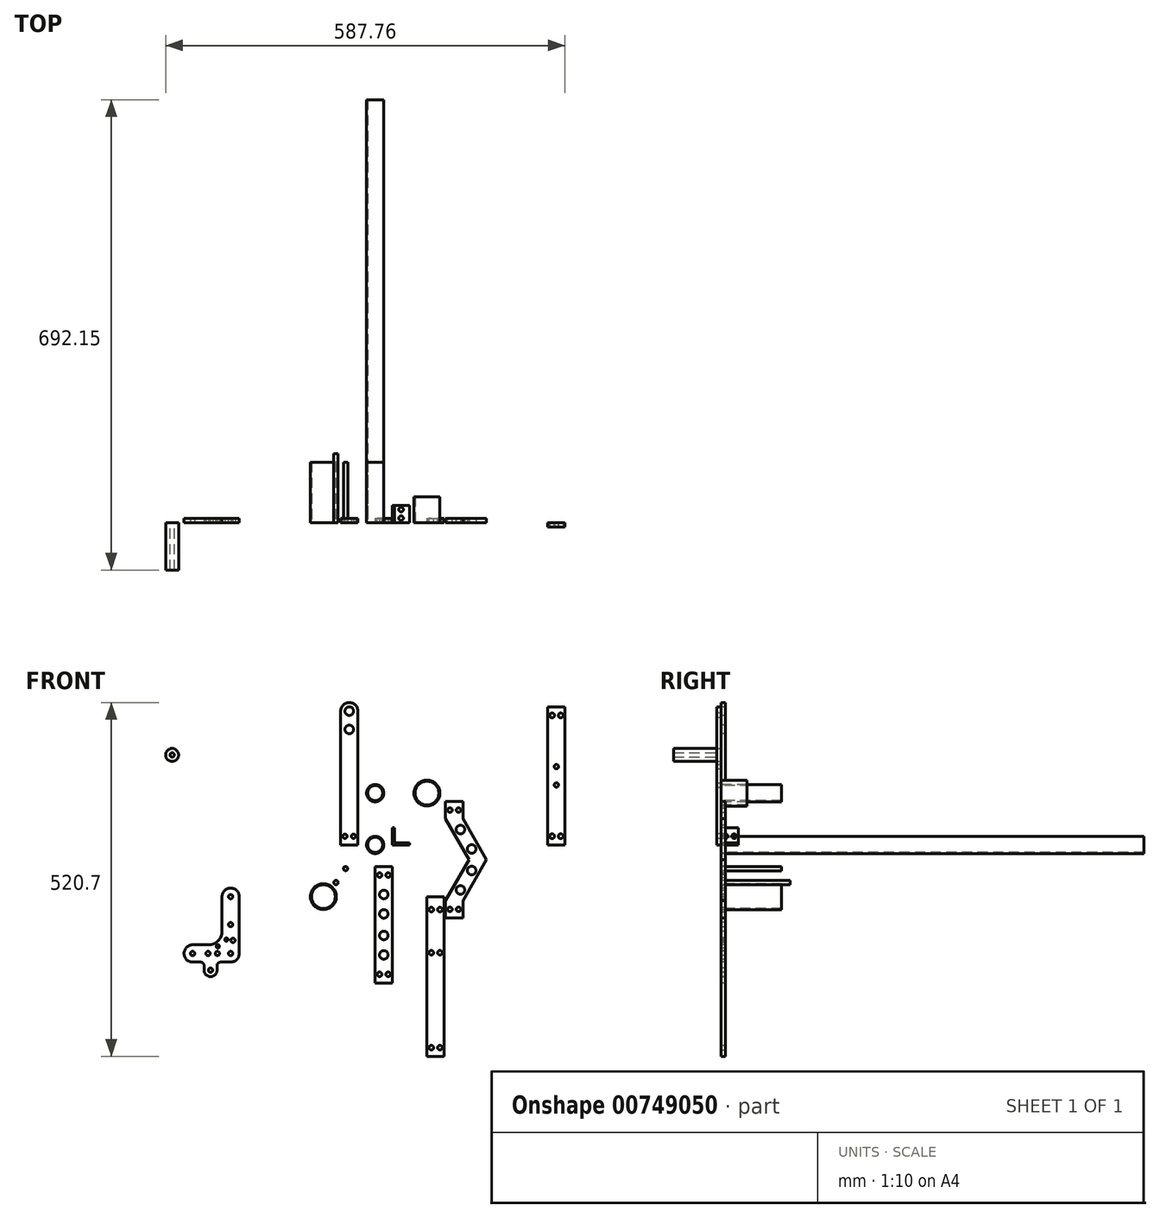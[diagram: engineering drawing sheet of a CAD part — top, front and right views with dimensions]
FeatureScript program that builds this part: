
annotation { "Feature Type Name" : "Feature", "Feature Type Description" : "" }
export const myFeature = defineFeature(function(context is Context, id is Id, definition is map)
    precondition{}
    {
        {
            var Q0;
            Q0=qCreatedBy(makeId("Front.planeOp"),FACE);
            var sketch = newSketch(context, id + "F0", { "sketchPlane" : qUnion([Q0])});
            skCircle(sketch, "E0", {"center": v(0, 0) * mm, "radius": 12.7 * mm});
            skCircle(sketch, "E1", {"center": v(0, 0) * mm, "radius": 11.11 * mm});
            skSolve(sketch);
        }
        {
            var Q0;
            Q0 = qSketchRegion(id + "F0", true);
            extrude(context, id + "F1", {"entities" : qUnion([Q0]), "oppositeDirection" : true, "depth" : 622.3 * mm, "offsetDistance" : 25.4 * mm});
        }
        {
            var Q0;
            Q0=qCreatedBy(makeId("Front.planeOp"),FACE);
            var sketch = newSketch(context, id + "F2", { "sketchPlane" : qUnion([Q0])});
            skCircle(sketch, "E2", {"center": v(76.2, 76.2) * mm, "radius": 19.05 * mm});
            skCircle(sketch, "E3", {"center": v(76.2, 76.2) * mm, "radius": 17.46 * mm});
            skSolve(sketch);
        }
        {
            var Q0;
            Q0 = qSketchRegion(id + "F2", true);
            extrude(context, id + "F3", {"entities" : qUnion([Q0]), "oppositeDirection" : true, "depth" : 38.1 * mm, "offsetDistance" : 25.4 * mm});
        }
        {
            var Q0;
            Q0=qCreatedBy(makeId("Front.planeOp"),FACE);
            var sketch = newSketch(context, id + "F4", { "sketchPlane" : qUnion([Q0])});
            skCircle(sketch, "E4", {"center": v(-76.2, -76.2) * mm, "radius": 19.05 * mm});
            skCircle(sketch, "E5", {"center": v(-76.2, -76.2) * mm, "radius": 17.46 * mm});
            skSolve(sketch);
        }
        {
            var Q0;
            Q0 = qSketchRegion(id + "F4", true);
            extrude(context, id + "F5", {"entities" : qUnion([Q0]), "oppositeDirection" : true, "depth" : 88.9 * mm, "offsetDistance" : 25.4 * mm});
        }
        {
            var Q0;
            Q0=qCreatedBy(makeId("Front.planeOp"),FACE);
            var sketch = newSketch(context, id + "F6", { "sketchPlane" : qUnion([Q0])});
            skLineSegment(sketch, "E6", {"start": v(-76.2, 12.7) * mm, "end": v(-76.2, 101.6) * mm});
            skLineSegment(sketch, "E7", {"start": v(-101.6, 101.6) * mm, "end": v(-101.6, 44.45) * mm});
            skLineSegment(sketch, "E8", {"start": v(-120.65, 25.4) * mm, "end": v(-146.05, 25.4) * mm});
            skLineSegment(sketch, "E9", {"start": v(-146.05, 0) * mm, "end": v(-88.9, 0) * mm});
            skCircle(sketch, "E10", {"center": v(-146.05, 12.7) * mm, "radius": 3.18 * mm});
            skArc(sketch, "E11", {"start": v(-146.05, 25.4) * mm, "mid": v(-158.75, 12.7) * mm, "end": v(-146.05, 0) * mm});
            skCircle(sketch, "E12", {"center": v(-88.9, 101.6) * mm, "radius": 3.18 * mm});
            skArc(sketch, "E13", {"start": v(-76.2, 101.6) * mm, "mid": v(-88.9, 114.3) * mm, "end": v(-101.6, 101.6) * mm});
            skCircle(sketch, "E14", {"center": v(-88.9, 12.7) * mm, "radius": 3.18 * mm});
            skArc(sketch, "E15", {"start": v(-88.9, 0) * mm, "mid": v(-79.92, 3.72) * mm, "end": v(-76.2, 12.7) * mm});
            skPoint(sketch, "E16.orphan", {"position": v(-76.2, 0) * mm});
            skPoint(sketch, "E17.visualSharp", {"position": v(-101.6, 25.4) * mm});
            skArc(sketch, "E17.filletArc", {"start": v(-120.65, 25.4) * mm, "mid": v(-107.18, 30.98) * mm, "end": v(-101.6, 44.45) * mm});
            skSolve(sketch);
        }
        {
            var Q0;
            Q0 = qSketchRegion(id + "F6", true);
            extrude(context, id + "F7", {"entities" : qUnion([Q0]), "oppositeDirection" : true, "depth" : 6.35 * mm, "offsetDistance" : 25.4 * mm});
        }
        {
            var Q0;
            Q0=qCreatedBy(makeId("Front.planeOp"),FACE);
            var sketch = newSketch(context, id + "F8", { "sketchPlane" : qUnion([Q0])});
            skLineSegment(sketch, "E18.bottom", {"start": v(-25.4, 0) * mm, "end": v(-50.8, 0) * mm});
            skLineSegment(sketch, "E18.left", {"start": v(-25.4, 0) * mm, "end": v(-25.4, 196.85) * mm});
            skLineSegment(sketch, "E18.right", {"start": v(-50.8, 0) * mm, "end": v(-50.8, 196.85) * mm});
            skArc(sketch, "E19", {"start": v(-25.4, 196.85) * mm, "mid": v(-38.1, 209.55) * mm, "end": v(-50.8, 196.85) * mm});
            skCircle(sketch, "E20", {"center": v(-38.1, 196.85) * mm, "radius": 6.35 * mm});
            skCircle(sketch, "E21", {"center": v(-38.1, 169.86) * mm, "radius": 6.35 * mm});
            skLineSegment(sketch, "E22", {"start": v(-38.1, 0) * mm, "end": v(-38.1, 209.55) * mm, "construction": true});
            skCircle(sketch, "E23", {"center": v(-44.45, 12.7) * mm, "radius": 3.18 * mm});
            skCircle(sketch, "E24.MirrorC", {"center": v(-31.75, 12.7) * mm, "radius": 3.18 * mm});
            skSolve(sketch);
        }
        {
            var Q0;
            Q0 = qSketchRegion(id + "F8", true);
            extrude(context, id + "F9", {"entities" : qUnion([Q0]), "oppositeDirection" : true, "depth" : 6.35 * mm, "offsetDistance" : 25.4 * mm});
        }
        {
            var Q0;
            Q0=qCreatedBy(makeId("Front.planeOp"),FACE);
            var sketch = newSketch(context, id + "F10", { "sketchPlane" : qUnion([Q0])});
            skLineSegment(sketch, "E25", {"start": v(25.4, 0) * mm, "end": v(25.4, 25.4) * mm});
            skLineSegment(sketch, "E26", {"start": v(25.4, 25.4) * mm, "end": v(28.58, 25.4) * mm});
            skLineSegment(sketch, "E27", {"start": v(28.58, 25.4) * mm, "end": v(28.58, 3.17) * mm});
            skLineSegment(sketch, "E28", {"start": v(28.58, 3.17) * mm, "end": v(50.8, 3.18) * mm});
            skLineSegment(sketch, "E29", {"start": v(50.8, 3.18) * mm, "end": v(50.8, 0) * mm});
            skLineSegment(sketch, "E30", {"start": v(50.8, 0) * mm, "end": v(25.4, 0) * mm});
            skSolve(sketch);
        }
        {
            var Q0;
            Q0 = qSketchRegion(id + "F10", true);
            extrude(context, id + "F11", {"entities" : qUnion([Q0]), "oppositeDirection" : true, "depth" : 25.4 * mm, "offsetDistance" : 25.4 * mm});
        }
        {
            var Q0;
            Q0=makeQuery(id+"F11.opExtrude","SWEPT_FACE",FACE,{"disambiguationData":[OSD([sQuery(id+"F10.wireOp",EDGE,"E25")])]});
            var sketch = newSketch(context, id + "F12", { "sketchPlane" : qUnion([Q0])});
            skLineSegment(sketch, "E31", {"start": v(-25.4, 12.7) * mm, "end": v(0, 12.7) * mm, "construction": true});
            skPoint(sketch, "E32", {"position": v(-19.05, 12.7) * mm});
            skPoint(sketch, "E33", {"position": v(-6.35, 12.7) * mm});
            skSolve(sketch);
        }
        {
            var Q0;
            Q0=makeQuery(id+"F11.opExtrude","SWEPT_FACE",FACE,{"disambiguationData":[OSD([sQuery(id+"F10.wireOp",EDGE,"E30")])]});
            var sketch = newSketch(context, id + "F13", { "sketchPlane" : qUnion([Q0])});
            skLineSegment(sketch, "E34", {"start": v(38.1, 0) * mm, "end": v(38.1, -25.4) * mm, "construction": true});
            skPoint(sketch, "E35", {"position": v(38.1, -6.35) * mm});
            skPoint(sketch, "E36", {"position": v(38.1, -19.05) * mm});
            skSolve(sketch);
        }
        {
            var Q0;
            Q0=sQuery(id+"F13.wireOp",VERTEX,"E35");
            var Q1;
            Q1=sQuery(id+"F13.wireOp",VERTEX,"E36");
            var Q2;
            Q2=sQuery(id+"F12.wireOp",VERTEX,"E32");
            var Q3;
            Q3=sQuery(id+"F12.wireOp",VERTEX,"E33");
            var Q4;
            Q4=makeQuery(id+"F11.opExtrude","SWEPT_BODY",BODY,{"disambiguationData":[OSD([sQuery(id+"F10.wireOp",EDGE,"E25"),sQuery(id+"F10.wireOp",EDGE,"E26"),sQuery(id+"F10.wireOp",EDGE,"E27"),sQuery(id+"F10.wireOp",EDGE,"E28"),sQuery(id+"F10.wireOp",EDGE,"E29"),sQuery(id+"F10.wireOp",EDGE,"E30")])]});
            hole(context, id + "F14", {"style" : HoleStyle.SIMPLE, "endStyle" : HoleEndStyle.BLIND, "standardTappedOrClearance" : lookupTablePath({ "standard" : "ANSI", "fit" : "Normal (ASME)", "size" : "1/4", "type" : "Clearance" }), "standardBlindInLast" : lookupTablePath({ "fit" : "Free", "standard" : "ANSI", "size" : "1/4", "type" : "Clearance" }), "holeDiameter" : 6.76 * mm, "majorDiameter" : 6.35 * mm, "holeDepth" : 3.17 * mm, "isTappedThrough" : true, "tappedDepth" : 22.25 * mm, "tapClearance" : 3, "locations" : qUnion([Q0, Q1, Q2, Q3]), "scope" : qUnion([Q4])});
        }
        {
            var Q0;
            Q0=qCreatedBy(makeId("Front.planeOp"),FACE);
            var sketch = newSketch(context, id + "F15", { "sketchPlane" : qUnion([Q0])});
            skCircle(sketch, "E37", {"center": v(0, 76.2) * mm, "radius": 12.7 * mm});
            skCircle(sketch, "E38", {"center": v(0, 76.2) * mm, "radius": 11.11 * mm});
            skSolve(sketch);
        }
        {
            var Q0;
            Q0 = qSketchRegion(id + "F15", true);
            extrude(context, id + "F16", {"entities" : qUnion([Q0]), "oppositeDirection" : true, "depth" : 88.9 * mm, "offsetDistance" : 25.4 * mm});
        }
        {
            var Q0;
            Q0=qCreatedBy(makeId("Front.planeOp"),FACE);
            var sketch = newSketch(context, id + "F17", { "sketchPlane" : qUnion([Q0])});
            skLineSegment(sketch, "E39.left", {"start": v(0, -76.2) * mm, "end": v(0, -158.75) * mm});
            skLineSegment(sketch, "E39.right", {"start": v(25.4, -69.85) * mm, "end": v(25.4, -165.1) * mm});
            skCircle(sketch, "E40", {"center": v(12.7, -73.03) * mm, "radius": 6.35 * mm});
            skCircle(sketch, "E41", {"center": v(12.7, -101.6) * mm, "radius": 6.35 * mm});
            skLineSegment(sketch, "E42", {"start": v(0, -117.48) * mm, "end": v(25.4, -117.48) * mm, "construction": true});
            skCircle(sketch, "E43.MirrorC", {"center": v(12.7, -133.35) * mm, "radius": 6.35 * mm});
            skCircle(sketch, "E44.MirrorC", {"center": v(12.7, -161.93) * mm, "radius": 6.35 * mm});
            skPoint(sketch, "E45.MirrorCS.end.orphan", {"position": v(0, -158.75) * mm});
            skPoint(sketch, "E45.MirrorCS.start.orphan", {"position": v(25.4, -165.1) * mm});
            skLineSegment(sketch, "E46", {"start": v(0, -76.2) * mm, "end": v(0, -31.75) * mm});
            skLineSegment(sketch, "E47", {"start": v(0, -31.75) * mm, "end": v(25.4, -31.75) * mm});
            skLineSegment(sketch, "E48", {"start": v(25.4, -31.75) * mm, "end": v(25.4, -69.85) * mm});
            skLineSegment(sketch, "E49", {"start": v(0, -158.75) * mm, "end": v(0, -203.2) * mm});
            skLineSegment(sketch, "E50", {"start": v(0, -203.2) * mm, "end": v(25.4, -203.2) * mm});
            skLineSegment(sketch, "E51", {"start": v(25.4, -203.2) * mm, "end": v(25.4, -165.1) * mm});
            skLineSegment(sketch, "E52", {"start": v(12.7, -31.75) * mm, "end": v(12.7, -203.2) * mm, "construction": true});
            skLineSegment(sketch, "E53", {"start": v(0, -44.45) * mm, "end": v(25.4, -44.45) * mm, "construction": true});
            skPoint(sketch, "E54", {"position": v(6.35, -44.45) * mm});
            skPoint(sketch, "E55.MirrorP", {"position": v(19.05, -44.45) * mm});
            skPoint(sketch, "E56.MirrorP", {"position": v(19.05, -190.5) * mm});
            skPoint(sketch, "E57.MirrorP", {"position": v(6.35, -190.5) * mm});
            skLineSegment(sketch, "E58", {"start": v(177.8, -205.28) * mm, "end": v(203.2, -205.28) * mm});
            skLineSegment(sketch, "E59", {"start": v(203.2, -205.28) * mm, "end": v(203.2, -179.88) * mm});
            skLineSegment(sketch, "E60", {"start": v(203.2, -179.88) * mm, "end": v(238.03, -119.56) * mm});
            skLineSegment(sketch, "E61", {"start": v(238.03, -119.56) * mm, "end": v(212.63, -119.56) * mm, "construction": true});
            skLineSegment(sketch, "E62", {"start": v(212.63, -119.56) * mm, "end": v(177.8, -179.88) * mm});
            skLineSegment(sketch, "E63", {"start": v(177.8, -179.88) * mm, "end": v(177.8, -205.28) * mm});
            skLineSegment(sketch, "E64", {"start": v(190.5, -205.28) * mm, "end": v(190.5, -179.88) * mm, "construction": true});
            skLineSegment(sketch, "E65", {"start": v(190.5, -179.88) * mm, "end": v(225.33, -119.56) * mm, "construction": true});
            skCircle(sketch, "E66", {"center": v(199.67, -164) * mm, "radius": 6.35 * mm});
            skCircle(sketch, "E67", {"center": v(216.16, -135.43) * mm, "radius": 6.35 * mm});
            skPoint(sketch, "E68", {"position": v(184.15, -192.58) * mm});
            skPoint(sketch, "E69.MirrorP", {"position": v(196.85, -192.58) * mm});
            skLineSegment(sketch, "E70.MirrorCS", {"start": v(203.2, -59.23) * mm, "end": v(238.03, -119.56) * mm});
            skLineSegment(sketch, "E71.MirrorCS", {"start": v(212.63, -119.56) * mm, "end": v(177.8, -59.23) * mm});
            skLineSegment(sketch, "E72.MirrorCS", {"start": v(190.5, -59.23) * mm, "end": v(225.33, -119.56) * mm, "construction": true});
            skCircle(sketch, "E73.MirrorC", {"center": v(216.16, -103.68) * mm, "radius": 6.35 * mm});
            skCircle(sketch, "E74.MirrorC", {"center": v(199.67, -75.1) * mm, "radius": 6.35 * mm});
            skLineSegment(sketch, "E75.MirrorCS", {"start": v(203.2, -33.83) * mm, "end": v(203.2, -59.23) * mm});
            skPoint(sketch, "E76.MirrorP", {"position": v(196.85, -46.53) * mm});
            skLineSegment(sketch, "E77.MirrorCS", {"start": v(190.5, -33.83) * mm, "end": v(190.5, -59.23) * mm, "construction": true});
            skPoint(sketch, "E78.MirrorP", {"position": v(184.15, -46.53) * mm});
            skLineSegment(sketch, "E79.MirrorCS", {"start": v(177.8, -59.23) * mm, "end": v(177.8, -33.83) * mm});
            skLineSegment(sketch, "E80.MirrorCS", {"start": v(177.8, -33.83) * mm, "end": v(203.2, -33.83) * mm});
            skLineSegment(sketch, "E81", {"start": v(212.98, -149.9) * mm, "end": v(238.38, -149.9) * mm});
            skLineSegment(sketch, "E82", {"start": v(238.38, -149.9) * mm, "end": v(238.38, -124.5) * mm});
            skLineSegment(sketch, "E83", {"start": v(238.38, -124.5) * mm, "end": v(273.21, -64.17) * mm});
            skLineSegment(sketch, "E84", {"start": v(273.21, -64.17) * mm, "end": v(247.81, -64.17) * mm, "construction": true});
            skLineSegment(sketch, "E85", {"start": v(247.81, -64.17) * mm, "end": v(212.98, -124.5) * mm});
            skLineSegment(sketch, "E86", {"start": v(212.98, -124.5) * mm, "end": v(212.98, -149.9) * mm});
            skLineSegment(sketch, "E87", {"start": v(225.68, -149.9) * mm, "end": v(225.68, -124.5) * mm, "construction": true});
            skLineSegment(sketch, "E88", {"start": v(225.68, -124.5) * mm, "end": v(260.51, -64.17) * mm, "construction": true});
            skCircle(sketch, "E89", {"center": v(234.85, -108.62) * mm, "radius": 6.35 * mm});
            skCircle(sketch, "E90", {"center": v(251.35, -80.04) * mm, "radius": 6.35 * mm});
            skPoint(sketch, "E91", {"position": v(219.33, -137.2) * mm});
            skPoint(sketch, "E92.MirrorP", {"position": v(232.03, -137.2) * mm});
            skLineSegment(sketch, "E93.MirrorCS", {"start": v(238.38, -3.84) * mm, "end": v(273.21, -64.17) * mm});
            skLineSegment(sketch, "E94.MirrorCS", {"start": v(247.81, -64.17) * mm, "end": v(212.98, -3.84) * mm});
            skLineSegment(sketch, "E95.MirrorCS", {"start": v(225.68, -3.84) * mm, "end": v(260.51, -64.17) * mm, "construction": true});
            skCircle(sketch, "E96.MirrorC", {"center": v(251.35, -48.3) * mm, "radius": 6.35 * mm});
            skCircle(sketch, "E97.MirrorC", {"center": v(234.85, -19.72) * mm, "radius": 6.35 * mm});
            skLineSegment(sketch, "E98.MirrorCS", {"start": v(238.38, 21.56) * mm, "end": v(238.38, -3.84) * mm});
            skPoint(sketch, "E99.MirrorP", {"position": v(232.03, 8.86) * mm});
            skLineSegment(sketch, "E100.MirrorCS", {"start": v(225.68, 21.56) * mm, "end": v(225.68, -3.84) * mm, "construction": true});
            skPoint(sketch, "E101.MirrorP", {"position": v(219.33, 8.86) * mm});
            skLineSegment(sketch, "E102.MirrorCS", {"start": v(212.98, -3.84) * mm, "end": v(212.98, 21.56) * mm});
            skLineSegment(sketch, "E103.MirrorCS", {"start": v(212.98, 21.56) * mm, "end": v(238.38, 21.56) * mm});
            skSolve(sketch);
        }
        {
            var Q0;
            Q0=makeQuery(id+"F17.imprint","IMPRINT",FACE,{"disambiguationData":[TD([[makeQuery(id+"F17.imprint","IMPRINT",EDGE,{"derivedFrom":sQuery(id+"F17.wireOp",EDGE,"E39.left")}),1.0]])]});
            extrude(context, id + "F18", {"entities" : qUnion([Q0]), "oppositeDirection" : true, "depth" : 6.35 * mm, "offsetDistance" : 25.4 * mm});
        }
        {
            var Q0;
            Q0=sQuery(id+"F17.wireOp",VERTEX,"E54");
            var Q1;
            Q1=sQuery(id+"F17.wireOp",VERTEX,"E55.MirrorP");
            var Q2;
            Q2=sQuery(id+"F17.wireOp",VERTEX,"E57.MirrorP");
            var Q3;
            Q3=sQuery(id+"F17.wireOp",VERTEX,"E56.MirrorP");
            var Q4;
            Q4=makeQuery(id+"F18.opExtrude","SWEPT_BODY",BODY,{"disambiguationData":[OSD([sQuery(id+"F17.wireOp",EDGE,"E39.left"),sQuery(id+"F17.wireOp",EDGE,"E39.right"),sQuery(id+"F17.wireOp",EDGE,"E40"),sQuery(id+"F17.wireOp",EDGE,"E41"),sQuery(id+"F17.wireOp",EDGE,"E43.MirrorC"),sQuery(id+"F17.wireOp",EDGE,"E44.MirrorC"),sQuery(id+"F17.wireOp",EDGE,"E46"),sQuery(id+"F17.wireOp",EDGE,"E47"),sQuery(id+"F17.wireOp",EDGE,"E48"),sQuery(id+"F17.wireOp",EDGE,"E49"),sQuery(id+"F17.wireOp",EDGE,"E50"),sQuery(id+"F17.wireOp",EDGE,"E51")])]});
            hole(context, id + "F19", {"style" : HoleStyle.SIMPLE, "endStyle" : HoleEndStyle.BLIND, "standardTappedOrClearance" : lookupTablePath({ "fit" : "Normal (ASME)", "standard" : "ANSI", "size" : "1/4", "type" : "Clearance" }), "standardBlindInLast" : lookupTablePath({ "fit" : "Free", "standard" : "ANSI", "size" : "1/4", "type" : "Clearance" }), "holeDiameter" : 6.76 * mm, "majorDiameter" : 6.35 * mm, "holeDepth" : 26.06 * mm, "isTappedThrough" : true, "tappedDepth" : 22.25 * mm, "tapClearance" : 3, "locations" : qUnion([Q0, Q1, Q2, Q3]), "scope" : qUnion([Q4])});
        }
        {
            var Q0;
            Q0=qCreatedBy(makeId("Front.planeOp"),FACE);
            var sketch = newSketch(context, id + "F20", { "sketchPlane" : qUnion([Q0])});
            skLineSegment(sketch, "E104.bottom", {"start": v(76.2, -76.2) * mm, "end": v(101.6, -76.2) * mm});
            skLineSegment(sketch, "E104.top", {"start": v(76.2, -311.15) * mm, "end": v(101.6, -311.15) * mm});
            skLineSegment(sketch, "E104.left", {"start": v(76.2, -76.2) * mm, "end": v(76.2, -311.15) * mm});
            skLineSegment(sketch, "E104.right", {"start": v(101.6, -76.2) * mm, "end": v(101.6, -311.15) * mm});
            skLineSegment(sketch, "E105", {"start": v(88.9, -76.2) * mm, "end": v(88.9, -311.15) * mm, "construction": true});
            skPoint(sketch, "E106", {"position": v(82.55, -95.25) * mm});
            skPoint(sketch, "E107", {"position": v(82.55, -298.45) * mm});
            skPoint(sketch, "E108", {"position": v(82.55, -158.75) * mm});
            skPoint(sketch, "E109.MirrorP", {"position": v(95.25, -95.25) * mm});
            skPoint(sketch, "E110.MirrorP", {"position": v(95.25, -158.75) * mm});
            skPoint(sketch, "E111.MirrorP", {"position": v(95.25, -298.45) * mm});
            skSolve(sketch);
        }
        {
            var Q0;
            Q0 = qSketchRegion(id + "F20", true);
            extrude(context, id + "F21", {"entities" : qUnion([Q0]), "oppositeDirection" : true, "depth" : 6.35 * mm, "offsetDistance" : 25.4 * mm});
        }
        {
            var Q0;
            Q0=sQuery(id+"F20.wireOp",VERTEX,"E106");
            var Q1;
            Q1=sQuery(id+"F20.wireOp",VERTEX,"E109.MirrorP");
            var Q2;
            Q2=sQuery(id+"F20.wireOp",VERTEX,"E108");
            var Q3;
            Q3=sQuery(id+"F20.wireOp",VERTEX,"E110.MirrorP");
            var Q4;
            Q4=sQuery(id+"F20.wireOp",VERTEX,"E107");
            var Q5;
            Q5=sQuery(id+"F20.wireOp",VERTEX,"E111.MirrorP");
            var Q6;
            Q6=makeQuery(id+"F21.opExtrude","SWEPT_BODY",BODY,{"disambiguationData":[OSD([sQuery(id+"F20.wireOp",EDGE,"E104.bottom"),sQuery(id+"F20.wireOp",EDGE,"E104.top"),sQuery(id+"F20.wireOp",EDGE,"E104.left"),sQuery(id+"F20.wireOp",EDGE,"E104.right")])]});
            hole(context, id + "F22", {"style" : HoleStyle.SIMPLE, "endStyle" : HoleEndStyle.BLIND, "standardTappedOrClearance" : lookupTablePath({ "fit" : "Normal (ASME)", "standard" : "ANSI", "size" : "1/4", "type" : "Clearance" }), "standardBlindInLast" : lookupTablePath({ "fit" : "Free", "standard" : "ANSI", "size" : "1/4", "type" : "Clearance" }), "holeDiameter" : 6.76 * mm, "majorDiameter" : 6.35 * mm, "holeDepth" : 26.06 * mm, "isTappedThrough" : true, "tappedDepth" : 22.25 * mm, "tapClearance" : 3, "locations" : qUnion([Q0, Q1, Q2, Q3, Q4, Q5]), "scope" : qUnion([Q6])});
        }
        {
            var Q0;
            Q0=qCreatedBy(makeId("Front.planeOp"),FACE);
            var sketch = newSketch(context, id + "F23", { "sketchPlane" : qUnion([Q0])});
            skLineSegment(sketch, "E112", {"start": v(103.66, -107.61) * mm, "end": v(129.06, -107.61) * mm});
            skLineSegment(sketch, "E113", {"start": v(129.06, -107.61) * mm, "end": v(129.06, -82.21) * mm});
            skLineSegment(sketch, "E114", {"start": v(129.06, -82.21) * mm, "end": v(163.88, -21.89) * mm});
            skLineSegment(sketch, "E115", {"start": v(163.88, -21.89) * mm, "end": v(138.48, -21.89) * mm, "construction": true});
            skLineSegment(sketch, "E116", {"start": v(138.48, -21.89) * mm, "end": v(103.66, -82.21) * mm});
            skLineSegment(sketch, "E117", {"start": v(103.66, -82.21) * mm, "end": v(103.66, -107.61) * mm});
            skLineSegment(sketch, "E118", {"start": v(116.36, -107.61) * mm, "end": v(116.36, -82.21) * mm, "construction": true});
            skLineSegment(sketch, "E119", {"start": v(116.36, -82.21) * mm, "end": v(151.18, -21.89) * mm, "construction": true});
            skCircle(sketch, "E120", {"center": v(125.52, -66.34) * mm, "radius": 6.35 * mm});
            skCircle(sketch, "E121", {"center": v(142.02, -37.76) * mm, "radius": 6.35 * mm});
            skPoint(sketch, "E122", {"position": v(110, -94.91) * mm});
            skPoint(sketch, "E123.MirrorP", {"position": v(122.7, -94.91) * mm});
            skLineSegment(sketch, "E124.MirrorCS", {"start": v(129.06, 38.44) * mm, "end": v(163.88, -21.89) * mm});
            skLineSegment(sketch, "E125.MirrorCS", {"start": v(138.48, -21.89) * mm, "end": v(103.66, 38.44) * mm});
            skLineSegment(sketch, "E126.MirrorCS", {"start": v(116.36, 38.44) * mm, "end": v(151.18, -21.89) * mm, "construction": true});
            skCircle(sketch, "E127.MirrorC", {"center": v(142.02, -6.01) * mm, "radius": 6.35 * mm});
            skCircle(sketch, "E128.MirrorC", {"center": v(125.52, 22.56) * mm, "radius": 6.35 * mm});
            skLineSegment(sketch, "E129.MirrorCS", {"start": v(129.06, 63.84) * mm, "end": v(129.06, 38.44) * mm});
            skPoint(sketch, "E130.MirrorP", {"position": v(122.7, 51.14) * mm});
            skLineSegment(sketch, "E131.MirrorCS", {"start": v(116.36, 63.84) * mm, "end": v(116.36, 38.44) * mm, "construction": true});
            skPoint(sketch, "E132.MirrorP", {"position": v(110, 51.14) * mm});
            skLineSegment(sketch, "E133.MirrorCS", {"start": v(103.66, 38.44) * mm, "end": v(103.66, 63.84) * mm});
            skLineSegment(sketch, "E134.MirrorCS", {"start": v(103.66, 63.84) * mm, "end": v(129.06, 63.84) * mm});
            skSolve(sketch);
        }
        {
            var Q0;
            Q0 = qSketchRegion(id + "F23", true);
            extrude(context, id + "F24", {"entities" : qUnion([Q0]), "oppositeDirection" : true, "depth" : 6.35 * mm, "offsetDistance" : 25.4 * mm});
        }
        {
            var Q0;
            Q0=sQuery(id+"F23.wireOp",VERTEX,"E122");
            var Q1;
            Q1=sQuery(id+"F23.wireOp",VERTEX,"E123.MirrorP");
            var Q2;
            Q2=sQuery(id+"F23.wireOp",VERTEX,"E132.MirrorP");
            var Q3;
            Q3=sQuery(id+"F23.wireOp",VERTEX,"E130.MirrorP");
            var Q4;
            Q4=makeQuery(id+"F24.opExtrude","SWEPT_BODY",BODY,{"disambiguationData":[OSD([sQuery(id+"F23.wireOp",EDGE,"E112"),sQuery(id+"F23.wireOp",EDGE,"E113"),sQuery(id+"F23.wireOp",EDGE,"E114"),sQuery(id+"F23.wireOp",EDGE,"E116"),sQuery(id+"F23.wireOp",EDGE,"E117"),sQuery(id+"F23.wireOp",EDGE,"E120"),sQuery(id+"F23.wireOp",EDGE,"E121"),sQuery(id+"F23.wireOp",EDGE,"E124.MirrorCS"),sQuery(id+"F23.wireOp",EDGE,"E125.MirrorCS"),sQuery(id+"F23.wireOp",EDGE,"E127.MirrorC"),sQuery(id+"F23.wireOp",EDGE,"E128.MirrorC"),sQuery(id+"F23.wireOp",EDGE,"E129.MirrorCS"),sQuery(id+"F23.wireOp",EDGE,"E133.MirrorCS"),sQuery(id+"F23.wireOp",EDGE,"E134.MirrorCS")])]});
            hole(context, id + "F25", {"style" : HoleStyle.SIMPLE, "endStyle" : HoleEndStyle.BLIND, "standardTappedOrClearance" : lookupTablePath({ "fit" : "Normal (ASME)", "standard" : "ANSI", "size" : "1/4", "type" : "Clearance" }), "standardBlindInLast" : lookupTablePath({ "fit" : "Free", "standard" : "ANSI", "size" : "1/4", "type" : "Clearance" }), "holeDiameter" : 6.76 * mm, "majorDiameter" : 6.35 * mm, "holeDepth" : 26.06 * mm, "isTappedThrough" : true, "tappedDepth" : 22.25 * mm, "tapClearance" : 3, "locations" : qUnion([Q0, Q1, Q2, Q3]), "scope" : qUnion([Q4])});
        }
        {
            var Q0;
            Q0=qCreatedBy(makeId("Front.planeOp"),FACE);
            var sketch = newSketch(context, id + "F26", { "sketchPlane" : qUnion([Q0])});
            skLineSegment(sketch, "E135", {"start": v(-200, -76.2) * mm, "end": v(-200, -159.9) * mm});
            skLineSegment(sketch, "E136", {"start": v(-212.7, -172.6) * mm, "end": v(-227.78, -172.6) * mm});
            skLineSegment(sketch, "E137", {"start": v(-232.78, -177.6) * mm, "end": v(-232.78, -184.42) * mm});
            skArc(sketch, "E138", {"start": v(-232.78, -184.42) * mm, "mid": v(-242.3, -193.95) * mm, "end": v(-251.84, -184.42) * mm});
            skLineSegment(sketch, "E139", {"start": v(-251.84, -184.42) * mm, "end": v(-251.84, -177.6) * mm});
            skLineSegment(sketch, "E140", {"start": v(-256.84, -172.6) * mm, "end": v(-268.7, -172.6) * mm});
            skArc(sketch, "E141", {"start": v(-268.7, -172.6) * mm, "mid": v(-281.4, -159.9) * mm, "end": v(-268.7, -147.2) * mm});
            skLineSegment(sketch, "E142", {"start": v(-268.7, -147.2) * mm, "end": v(-245.4, -147.2) * mm});
            skLineSegment(sketch, "E143", {"start": v(-225.4, -127.2) * mm, "end": v(-225.4, -76.2) * mm});
            skArc(sketch, "E144", {"start": v(-225.4, -76.2) * mm, "mid": v(-212.7, -63.5) * mm, "end": v(-200, -76.2) * mm});
            skPoint(sketch, "E145.visualSharp", {"position": v(-200, -172.6) * mm});
            skArc(sketch, "E145.filletArc", {"start": v(-212.7, -172.6) * mm, "mid": v(-203.72, -168.88) * mm, "end": v(-200, -159.9) * mm});
            skPoint(sketch, "E146.visualSharp", {"position": v(-225.4, -147.2) * mm});
            skArc(sketch, "E146.filletArc", {"start": v(-245.4, -147.2) * mm, "mid": v(-231.26, -141.34) * mm, "end": v(-225.4, -127.2) * mm});
            skPoint(sketch, "E147.visualSharp", {"position": v(-251.84, -172.6) * mm});
            skArc(sketch, "E147.filletArc", {"start": v(-251.84, -177.6) * mm, "mid": v(-253.3, -174.06) * mm, "end": v(-256.84, -172.6) * mm});
            skPoint(sketch, "E148.visualSharp", {"position": v(-232.78, -172.6) * mm});
            skArc(sketch, "E148.filletArc", {"start": v(-227.78, -172.6) * mm, "mid": v(-231.32, -174.06) * mm, "end": v(-232.78, -177.6) * mm});
            skLineSegment(sketch, "E149", {"start": v(-212.7, -63.5) * mm, "end": v(-212.7, -172.63) * mm, "construction": true});
            skLineSegment(sketch, "E150", {"start": v(-200, -159.9) * mm, "end": v(-281.4, -159.9) * mm, "construction": true});
            skCircle(sketch, "E151", {"center": v(-212.7, -76.2) * mm, "radius": 3.18 * mm});
            skCircle(sketch, "E152", {"center": v(-212.7, -159.9) * mm, "radius": 3.18 * mm});
            skCircle(sketch, "E153", {"center": v(-232.23, -159.9) * mm, "radius": 3.18 * mm});
            skCircle(sketch, "E154", {"center": v(-246.1, -159.9) * mm, "radius": 3.18 * mm});
            skCircle(sketch, "E155", {"center": v(-268.7, -159.9) * mm, "radius": 3.18 * mm});
            skCircle(sketch, "E156", {"center": v(-242.3, -184.42) * mm, "radius": 3.18 * mm});
            skCircle(sketch, "E157", {"center": v(-209.34, -140.64) * mm, "radius": 3.18 * mm});
            skCircle(sketch, "E158", {"center": v(-219, -139.4) * mm, "radius": 2.38 * mm});
            skCircle(sketch, "E159", {"center": v(-212.7, -117.4) * mm, "radius": 3.18 * mm});
            skCircle(sketch, "E160", {"center": v(-231.49, -149.41) * mm, "radius": 2.38 * mm});
            skSolve(sketch);
        }
        {
            var Q0;
            Q0=makeQuery(id+"F26.imprint","IMPRINT",FACE,{"disambiguationData":[TD([[makeQuery(id+"F26.imprint","IMPRINT",EDGE,{"derivedFrom":sQuery(id+"F26.wireOp",EDGE,"E135")}),-1.0]])]});
            extrude(context, id + "F27", {"entities" : qUnion([Q0]), "oppositeDirection" : true, "depth" : 6.35 * mm, "offsetDistance" : 25 * mm});
        }
        {
            var Q0;
            Q0=qCreatedBy(makeId("Front.planeOp"),FACE);
            var sketch = newSketch(context, id + "F28", { "sketchPlane" : qUnion([Q0])});
            skCircle(sketch, "E161", {"center": v(-57.68, -55.37) * mm, "radius": 3.18 * mm});
            skSolve(sketch);
        }
        {
            var Q0;
            Q0 = qSketchRegion(id + "F28", true);
            extrude(context, id + "F29", {"entities" : qUnion([Q0]), "oppositeDirection" : true, "depth" : 101.6 * mm, "offsetDistance" : 25.4 * mm});
        }
        {
            var Q0;
            Q0=qCreatedBy(makeId("Front.planeOp"),FACE);
            var sketch = newSketch(context, id + "F30", { "sketchPlane" : qUnion([Q0])});
            skCircle(sketch, "E162", {"center": v(-43.65, -34.92) * mm, "radius": 3.18 * mm});
            skSolve(sketch);
        }
        {
            var Q0;
            Q0 = qSketchRegion(id + "F30", true);
            extrude(context, id + "F31", {"entities" : qUnion([Q0]), "oppositeDirection" : true, "depth" : 88.9 * mm, "offsetDistance" : 25.4 * mm});
        }
        {
            var Q0;
            Q0=qCreatedBy(makeId("Front.planeOp"),FACE);
            var sketch = newSketch(context, id + "F32", { "sketchPlane" : qUnion([Q0])});
            skLineSegment(sketch, "E163.bottom", {"start": v(254, 203.2) * mm, "end": v(279.4, 203.2) * mm});
            skLineSegment(sketch, "E163.top", {"start": v(254, 0) * mm, "end": v(279.4, 0) * mm});
            skLineSegment(sketch, "E163.left", {"start": v(254, 203.2) * mm, "end": v(254, 0) * mm});
            skLineSegment(sketch, "E163.right", {"start": v(279.4, 203.2) * mm, "end": v(279.4, 0) * mm});
            skLineSegment(sketch, "E164", {"start": v(266.7, 203.2) * mm, "end": v(266.7, 0) * mm, "construction": true});
            skLineSegment(sketch, "E165", {"start": v(254, 101.6) * mm, "end": v(279.4, 101.6) * mm, "construction": true});
            skCircle(sketch, "E166", {"center": v(266.7, 115.1) * mm, "radius": 3.18 * mm});
            skPoint(sketch, "E167", {"position": v(260.35, 190.5) * mm});
            skPoint(sketch, "E168.MirrorP", {"position": v(273.05, 190.5) * mm});
            skLineSegment(sketch, "E169.MirrorCS", {"start": v(266.7, 0) * mm, "end": v(266.7, 203.2) * mm, "construction": true});
            skPoint(sketch, "E170.MirrorP", {"position": v(273.05, 12.7) * mm});
            skPoint(sketch, "E171.MirrorP", {"position": v(260.35, 12.7) * mm});
            skCircle(sketch, "E172.MirrorC", {"center": v(266.7, 88.1) * mm, "radius": 3.18 * mm});
            skSolve(sketch);
        }
        {
            var Q0;
            Q0 = qSketchRegion(id + "F32", true);
            extrude(context, id + "F33", {"entities" : qUnion([Q0]), "depth" : 6.35 * mm, "offsetDistance" : 25.4 * mm});
        }
        {
            var Q0;
            Q0=sQuery(id+"F32.wireOp",VERTEX,"E171.MirrorP");
            var Q1;
            Q1=sQuery(id+"F32.wireOp",VERTEX,"E170.MirrorP");
            var Q2;
            Q2=sQuery(id+"F32.wireOp",VERTEX,"E167");
            var Q3;
            Q3=sQuery(id+"F32.wireOp",VERTEX,"E168.MirrorP");
            var Q4;
            Q4=makeQuery(id+"F33.opExtrude","SWEPT_BODY",BODY,{"disambiguationData":[OSD([sQuery(id+"F32.wireOp",EDGE,"E163.bottom"),sQuery(id+"F32.wireOp",EDGE,"E163.top"),sQuery(id+"F32.wireOp",EDGE,"E163.left"),sQuery(id+"F32.wireOp",EDGE,"E163.right"),sQuery(id+"F32.wireOp",EDGE,"E166"),sQuery(id+"F32.wireOp",EDGE,"E172.MirrorC")])]});
            hole(context, id + "F34", {"style" : HoleStyle.SIMPLE, "endStyle" : HoleEndStyle.BLIND, "oppositeDirection" : true, "standardTappedOrClearance" : lookupTablePath({ "fit" : "Normal (ASME)", "standard" : "ANSI", "size" : "1/4", "type" : "Clearance" }), "standardBlindInLast" : lookupTablePath({ "fit" : "Normal", "standard" : "ANSI", "size" : "1/4", "type" : "Clearance" }), "holeDiameter" : 7.14 * mm, "majorDiameter" : 6.35 * mm, "holeDepth" : 304.8 * mm, "isTappedThrough" : true, "tappedDepth" : 301 * mm, "tapClearance" : 3, "locations" : qUnion([Q0, Q1, Q2, Q3]), "scope" : qUnion([Q4])});
        }
        {
            var Q0;
            Q0=makeQuery(id+"F7.opExtrude","SWEPT_BODY",BODY,{"disambiguationData":[OSD([sQuery(id+"F6.wireOp",EDGE,"E6"),sQuery(id+"F6.wireOp",EDGE,"E7"),sQuery(id+"F6.wireOp",EDGE,"E8"),sQuery(id+"F6.wireOp",EDGE,"E9"),sQuery(id+"F6.wireOp",EDGE,"E10"),sQuery(id+"F6.wireOp",EDGE,"E11"),sQuery(id+"F6.wireOp",EDGE,"E12"),sQuery(id+"F6.wireOp",EDGE,"E13"),sQuery(id+"F6.wireOp",EDGE,"E14"),sQuery(id+"F6.wireOp",EDGE,"E15"),sQuery(id+"F6.wireOp",EDGE,"E17.filletArc")])]});
            deleteBodies(context, id + "F35", {"entities" : qUnion([Q0])});
        }
        {
            var Q0;
            Q0=qCreatedBy(makeId("Front.planeOp"),FACE);
            var sketch = newSketch(context, id + "F36", { "sketchPlane" : qUnion([Q0])});
            skCircle(sketch, "E173", {"center": v(-298.84, 132.34) * mm, "radius": 9.53 * mm});
            skCircle(sketch, "E174", {"center": v(-298.84, 132.34) * mm, "radius": 3.18 * mm});
            skSolve(sketch);
        }
        {
            var Q0;
            Q0 = qSketchRegion(id + "F36", true);
            extrude(context, id + "F37", {"entities" : qUnion([Q0]), "depth" : 69.85 * mm, "offsetDistance" : 25.4 * mm});
        }
    });
